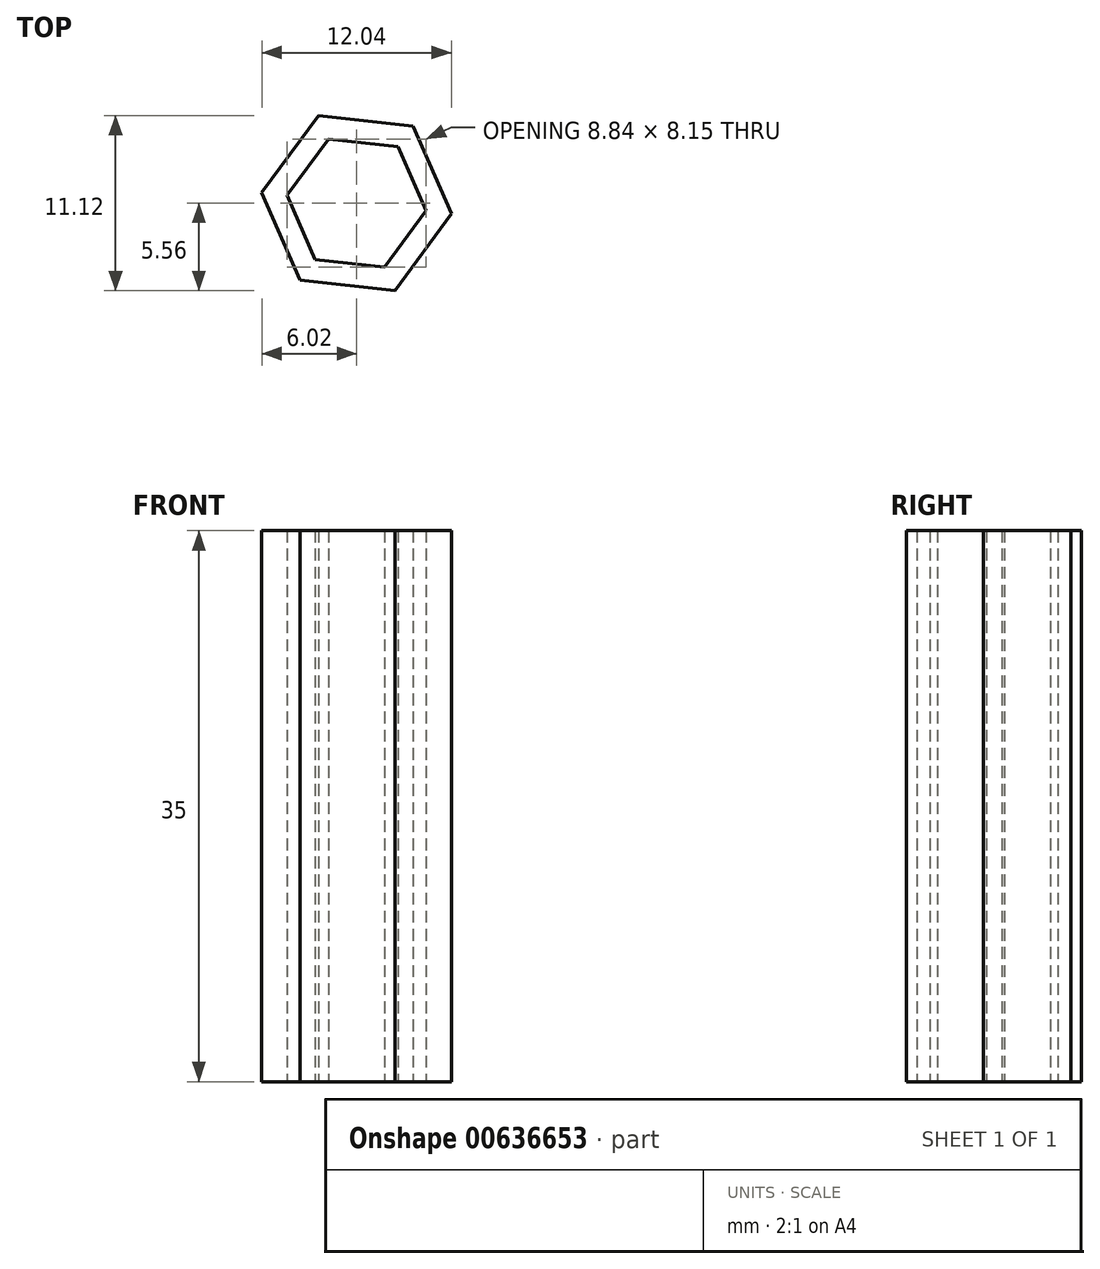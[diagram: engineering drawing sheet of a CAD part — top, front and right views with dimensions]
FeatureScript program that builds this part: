
annotation { "Feature Type Name" : "Feature", "Feature Type Description" : "" }
export const myFeature = defineFeature(function(context is Context, id is Id, definition is map)
    precondition{}
    {
        {
            var Q0;
            Q0=qCreatedBy(makeId("Top.planeOp"),FACE);
            var sketch = newSketch(context, id + "F0", { "sketchPlane" : qUnion([Q0])});
            skCircle(sketch, "E0.cCircle", {"center": v(0, 0) * mm, "radius": 3.85 * mm, "construction": true});
            skLineSegment(sketch, "E0.0", {"start": v(2.64, 3.58) * mm, "end": v(4.42, -0.5) * mm});
            skLineSegment(sketch, "E0.1", {"start": v(4.42, -0.5) * mm, "end": v(1.78, -4.07) * mm});
            skLineSegment(sketch, "E0.2", {"start": v(1.78, -4.07) * mm, "end": v(-2.64, -3.58) * mm});
            skLineSegment(sketch, "E0.3", {"start": v(-2.64, -3.58) * mm, "end": v(-4.42, 0.5) * mm});
            skLineSegment(sketch, "E0.4", {"start": v(-4.42, 0.5) * mm, "end": v(-1.78, 4.07) * mm});
            skLineSegment(sketch, "E0.5", {"start": v(-1.78, 4.07) * mm, "end": v(2.64, 3.58) * mm});
            skPoint(sketch, "E0.0.midPoint", {"position": v(3.53, 1.54) * mm});
            skCircle(sketch, "E1.cCircle", {"center": v(0, 0) * mm, "radius": 5.25 * mm, "construction": true});
            skLineSegment(sketch, "E1.0", {"start": v(-6.02, 0.68) * mm, "end": v(-2.43, 5.56) * mm});
            skLineSegment(sketch, "E1.1", {"start": v(-2.43, 5.56) * mm, "end": v(3.6, 4.88) * mm});
            skLineSegment(sketch, "E1.2", {"start": v(3.6, 4.88) * mm, "end": v(6.02, -0.68) * mm});
            skLineSegment(sketch, "E1.3", {"start": v(6.02, -0.68) * mm, "end": v(2.43, -5.56) * mm});
            skLineSegment(sketch, "E1.4", {"start": v(2.43, -5.56) * mm, "end": v(-3.6, -4.88) * mm});
            skLineSegment(sketch, "E1.5", {"start": v(-3.6, -4.88) * mm, "end": v(-6.02, 0.68) * mm});
            skPoint(sketch, "E1.0.midPoint", {"position": v(-4.23, 3.12) * mm});
            skLineSegment(sketch, "E2", {"start": v(-3.1, 2.28) * mm, "end": v(-4.23, 3.12) * mm});
            skSolve(sketch);
        }
        {
            var Q0;
            Q0 = qSketchRegion(id + "F0", true);
            extrude(context, id + "F1", {"entities" : qUnion([Q0]), "depth" : 35 * mm, "offsetDistance" : 25 * mm});
        }
    });
